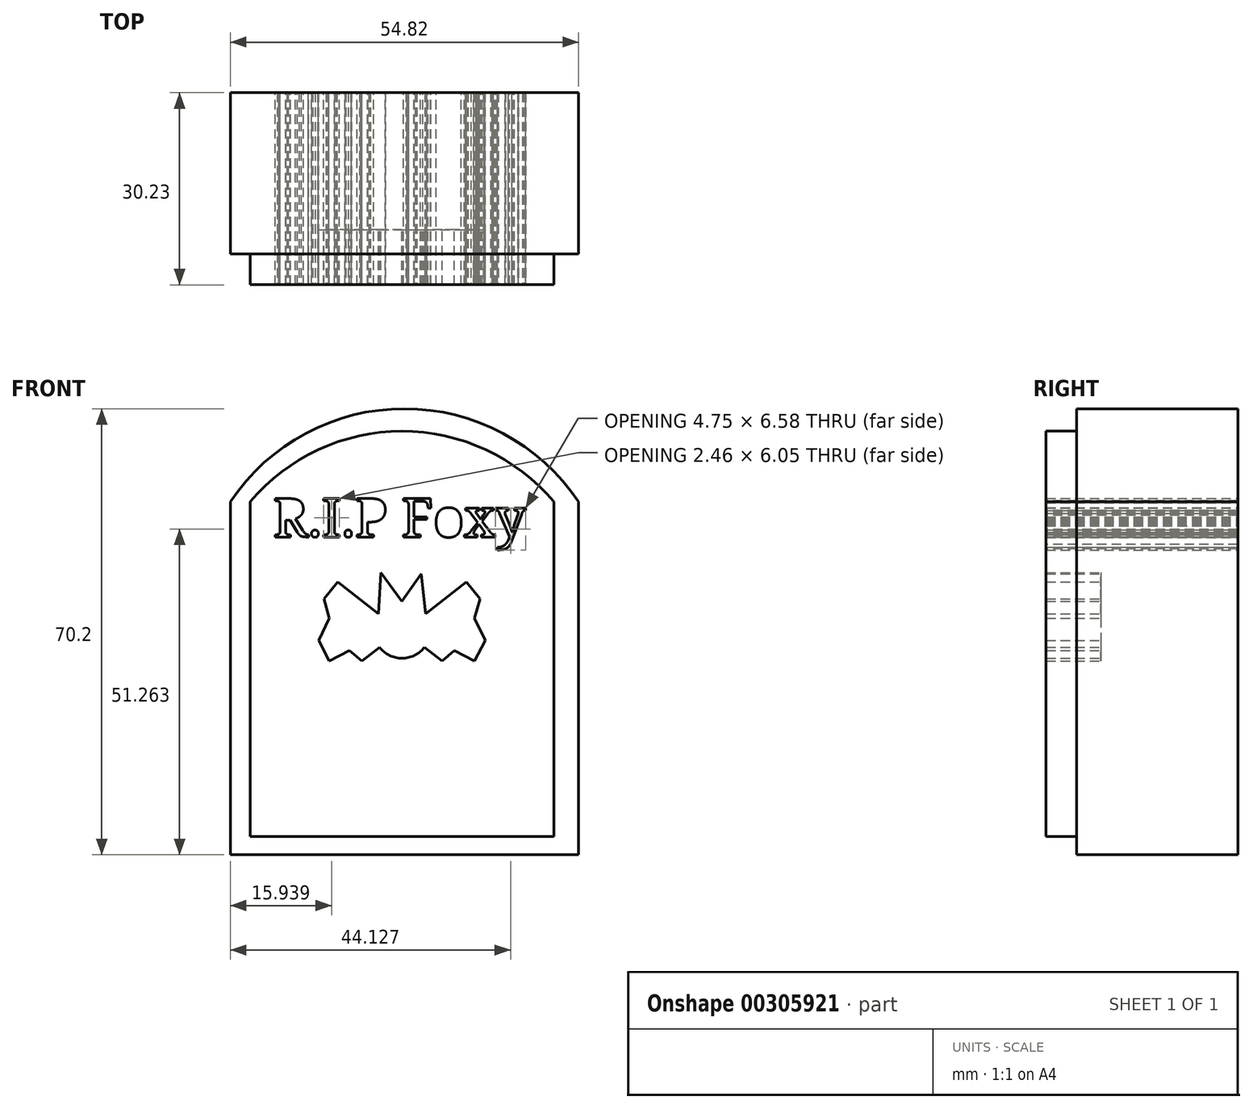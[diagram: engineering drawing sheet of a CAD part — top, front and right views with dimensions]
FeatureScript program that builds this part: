
annotation { "Feature Type Name" : "Feature", "Feature Type Description" : "" }
export const myFeature = defineFeature(function(context is Context, id is Id, definition is map)
    precondition{}
    {
        {
            var Q0;
            Q0=qCreatedBy(makeId("Front.planeOp"),FACE);
            var sketch = newSketch(context, id + "F0", { "sketchPlane" : qUnion([Q0])});
            skLineSegment(sketch, "E0", {"start": v(-28.44, 0) * mm, "end": v(-28.44, 55.55) * mm});
            skLineSegment(sketch, "E1", {"start": v(26.38, 0) * mm, "end": v(26.38, 55.55) * mm});
            skArc(sketch, "E2", {"start": v(26.38, 55.55) * mm, "mid": v(-1.03, 70.2) * mm, "end": v(-28.44, 55.55) * mm});
            skLineSegment(sketch, "E3", {"start": v(-28.44, 0) * mm, "end": v(26.38, 0) * mm});
            skLineSegment(sketch, "E4", {"start": v(-25.3, 55.55) * mm, "end": v(-25.3, 2.87) * mm});
            skLineSegment(sketch, "E5", {"start": v(-25.3, 2.87) * mm, "end": v(22.48, 2.87) * mm});
            skLineSegment(sketch, "E6", {"start": v(22.48, 2.87) * mm, "end": v(22.48, 55.55) * mm});
            skArc(sketch, "E7", {"start": v(22.48, 55.55) * mm, "mid": v(-1.41, 66.66) * mm, "end": v(-25.3, 55.55) * mm});
            skCircle(sketch, "E8", {"center": v(-1.41, 35.42) * mm, "radius": 4.5 * mm});
            skLineSegment(sketch, "E9", {"start": v(-5.14, 37.94) * mm, "end": v(-11.57, 42.97) * mm});
            skLineSegment(sketch, "E10", {"start": v(-11.57, 42.97) * mm, "end": v(-13.68, 40.26) * mm});
            skLineSegment(sketch, "E11", {"start": v(-13.68, 40.26) * mm, "end": v(-12.85, 37.25) * mm});
            skLineSegment(sketch, "E12", {"start": v(-12.85, 37.25) * mm, "end": v(-14.52, 33.72) * mm});
            skLineSegment(sketch, "E13", {"start": v(-14.52, 33.72) * mm, "end": v(-12.85, 30.48) * mm});
            skLineSegment(sketch, "E14", {"start": v(-12.85, 30.48) * mm, "end": v(-9.67, 32.11) * mm});
            skLineSegment(sketch, "E15", {"start": v(-9.67, 32.11) * mm, "end": v(-7.73, 30.48) * mm});
            skLineSegment(sketch, "E16", {"start": v(-7.73, 30.48) * mm, "end": v(-4.95, 32.65) * mm});
            skLineSegment(sketch, "E17", {"start": v(-1.41, 39.92) * mm, "end": v(-1.41, 30.93) * mm, "construction": true});
            skLineSegment(sketch, "E18.MirrorCS", {"start": v(10.02, 37.25) * mm, "end": v(11.69, 33.72) * mm});
            skLineSegment(sketch, "E19.MirrorCS", {"start": v(10.85, 40.26) * mm, "end": v(10.02, 37.25) * mm});
            skLineSegment(sketch, "E20.MirrorCS", {"start": v(8.74, 42.97) * mm, "end": v(10.85, 40.26) * mm});
            skLineSegment(sketch, "E21.MirrorCS", {"start": v(2.3, 37.94) * mm, "end": v(8.74, 42.97) * mm});
            skLineSegment(sketch, "E22.MirrorCS", {"start": v(4.9, 30.48) * mm, "end": v(2.12, 32.65) * mm});
            skLineSegment(sketch, "E23.MirrorCS", {"start": v(6.84, 32.11) * mm, "end": v(4.9, 30.48) * mm});
            skLineSegment(sketch, "E24.MirrorCS", {"start": v(10.02, 30.48) * mm, "end": v(6.84, 32.11) * mm});
            skLineSegment(sketch, "E25.MirrorCS", {"start": v(11.69, 33.72) * mm, "end": v(10.02, 30.48) * mm});
            skText(sketch, "E26", { "text": "R.I.P Foxy", "fontName": "NotoSerif-Regular.ttf"});
            skLineSegment(sketch, "E27", {"start": v(-1.41, 39.92) * mm, "end": v(1.63, 44.22) * mm});
            skLineSegment(sketch, "E28", {"start": v(1.63, 44.22) * mm, "end": v(2.3, 37.94) * mm});
            skLineSegment(sketch, "E29", {"start": v(-1.41, 39.92) * mm, "end": v(-4.76, 44.4) * mm});
            skLineSegment(sketch, "E30", {"start": v(-4.76, 44.4) * mm, "end": v(-5.14, 37.94) * mm});
            const initialGuessF0  = {"E26": [-0.02173, 0.05001, 1, 0, 0.0061]};
            skSetInitialGuess(sketch, initialGuessF0);
            skSolve(sketch);
        }
        {
            var Q0;
            Q0=makeQuery(id+"F0.imprint","IMPRINT",FACE,{"disambiguationData":[TD([[makeQuery(id+"F0.imprint","IMPRINT",EDGE,{"derivedFrom":sQuery(id+"F0.wireOp",EDGE,"E0")}),-1.0]])]});
            extrude(context, id + "F1", {"entities" : qUnion([Q0]), "depth" : 25.4 * mm});
        }
        {
            var Q0;
            Q0=makeQuery(id+"F0.imprint","IMPRINT",FACE,{"disambiguationData":[TD([[makeQuery(id+"F0.imprint","IMPRINT",EDGE,{"derivedFrom":sQuery(id+"F0.wireOp",EDGE,"E4")}),1.0]])]});
            extrude(context, id + "F2", {"entities" : qUnion([Q0]), "operationType" : NewBodyOperationType.ADD, "depth" : 30.23 * mm});
        }
        {
            var Q0;
            Q0 = qSketchRegion(id + "F0", true);
            var Q1;
            Q1=makeQuery(id+"F0.imprint","IMPRINT",FACE,{"disambiguationData":[TD([[makeQuery(id+"F0.imprint","IMPRINT",EDGE,{"derivedFrom":sQuery(id+"F0.wireOp",EDGE,"E18.MirrorCS")}),-1.0]])]});
            var Q2;
            {var subQ0=sQuery(id+"F0.wireOp",EDGE,"E8");var subQ1=makeQuery(id+"F0.imprint","INTERSECT",VERTEX,{"derivedFrom":[subQ0,sQuery(id+"F0.wireOp",EDGE,"E16")]});Q2=makeQuery(id+"F0.imprint","IMPRINT",FACE,{"disambiguationData":[TD([[makeQuery(id+"F0.imprint","IMPRINT",EDGE,{"disambiguationData":[TD([[subQ1,-1.0]])],"derivedFrom":subQ0}),1.0]])]});}
            var Q3;
            {var subQ2=sQuery(id+"F0.wireOp",EDGE,"E27");Q3=makeQuery(id+"F0.imprint","IMPRINT",FACE,{"disambiguationData":[TD([[makeQuery(id+"F0.imprint","IMPRINT",EDGE,{"derivedFrom":subQ2}),-1.0]])]});}
            var Q4;
            {var subQ2=sQuery(id+"F0.wireOp",EDGE,"E29");Q4=makeQuery(id+"F0.imprint","IMPRINT",FACE,{"disambiguationData":[TD([[makeQuery(id+"F0.imprint","IMPRINT",EDGE,{"derivedFrom":subQ2}),1.0]])]});}
            var Q5;
            {var subQ0=sQuery(id+"F0.wireOp",EDGE,"E9");Q5=makeQuery(id+"F0.imprint","IMPRINT",FACE,{"disambiguationData":[TD([[makeQuery(id+"F0.imprint","IMPRINT",EDGE,{"derivedFrom":subQ0}),1.0]])]});}
            extrude(context, id + "F3", {"entities" : qUnion([Q0, Q1, Q2, Q3, Q4, Q5]), "operationType" : NewBodyOperationType.ADD, "depth" : 21.59 * mm});
        }
    });
